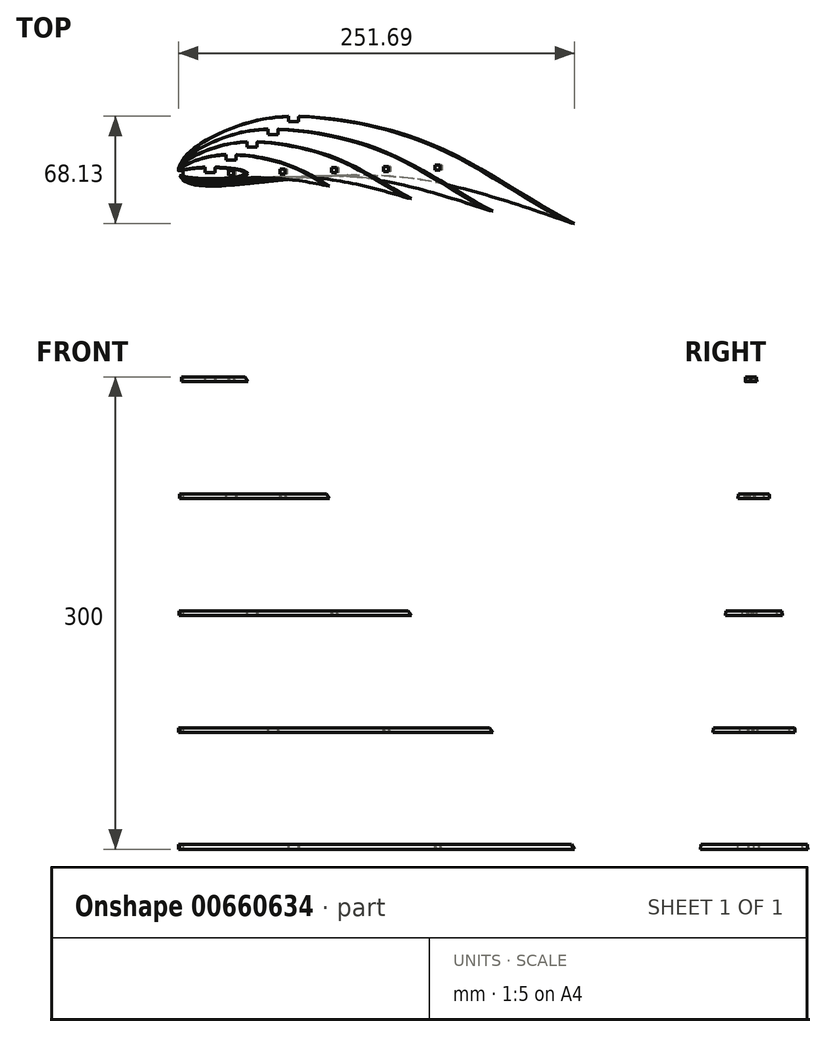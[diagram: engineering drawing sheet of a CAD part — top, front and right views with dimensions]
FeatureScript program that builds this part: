
annotation { "Feature Type Name" : "Feature", "Feature Type Description" : "" }
export const myFeature = defineFeature(function(context is Context, id is Id, definition is map)
    precondition{}
    {
        {
            var Q0;
            Q0=qCreatedBy(makeId("Top.planeOp"),FACE);
            var sketch = newSketch(context, id + "F0", { "sketchPlane" : qUnion([Q0])});
            skLineSegment(sketch, "E0", {"start": v(2.33, 8.6) * mm, "end": v(8.41, 14.52) * mm});
            skLineSegment(sketch, "E1", {"start": v(8.41, 14.52) * mm, "end": v(11.57, 17.3) * mm});
            skLineSegment(sketch, "E2", {"start": v(11.57, 17.3) * mm, "end": v(15.59, 20.39) * mm});
            skLineSegment(sketch, "E3", {"start": v(15.59, 20.39) * mm, "end": v(18.37, 22.2) * mm});
            skLineSegment(sketch, "E4", {"start": v(18.37, 22.2) * mm, "end": v(22.04, 24.25) * mm});
            skLineSegment(sketch, "E5", {"start": v(22.04, 24.25) * mm, "end": v(25.86, 26.05) * mm});
            skLineSegment(sketch, "E6", {"start": v(25.86, 26.05) * mm, "end": v(29.8, 27.65) * mm});
            skLineSegment(sketch, "E7", {"start": v(29.8, 27.65) * mm, "end": v(33.82, 29.05) * mm});
            skLineSegment(sketch, "E8", {"start": v(33.82, 29.05) * mm, "end": v(38.41, 30.45) * mm});
            skLineSegment(sketch, "E9", {"start": v(38.41, 30.45) * mm, "end": v(41.99, 31.4) * mm});
            skLineSegment(sketch, "E10", {"start": v(41.99, 31.4) * mm, "end": v(46.1, 32.39) * mm});
            skLineSegment(sketch, "E11", {"start": v(46.1, 32.39) * mm, "end": v(50.24, 33.24) * mm});
            skLineSegment(sketch, "E12", {"start": v(50.24, 33.24) * mm, "end": v(54.39, 33.98) * mm});
            skLineSegment(sketch, "E13", {"start": v(54.39, 33.98) * mm, "end": v(58.55, 34.6) * mm});
            skLineSegment(sketch, "E14", {"start": v(58.55, 34.6) * mm, "end": v(62.73, 35.1) * mm});
            skLineSegment(sketch, "E15", {"start": v(62.73, 35.1) * mm, "end": v(68.1, 35.6) * mm});
            skLineSegment(sketch, "E16", {"start": v(68.1, 35.6) * mm, "end": v(79.58, 36.1) * mm});
            skLineSegment(sketch, "E17", {"start": v(79.58, 36.1) * mm, "end": v(88.03, 36) * mm});
            skLineSegment(sketch, "E18", {"start": v(88.03, 36) * mm, "end": v(96.45, 35.47) * mm});
            skLineSegment(sketch, "E19", {"start": v(96.45, 35.47) * mm, "end": v(102.22, 34.87) * mm});
            skLineSegment(sketch, "E20", {"start": v(102.22, 34.87) * mm, "end": v(113.1, 33.19) * mm});
            skLineSegment(sketch, "E21", {"start": v(113.1, 33.19) * mm, "end": v(121.32, 31.46) * mm});
            skLineSegment(sketch, "E22", {"start": v(121.32, 31.46) * mm, "end": v(129.5, 29.38) * mm});
            skLineSegment(sketch, "E23", {"start": v(129.5, 29.38) * mm, "end": v(137.56, 27.01) * mm});
            skLineSegment(sketch, "E24", {"start": v(137.56, 27.01) * mm, "end": v(145.85, 24.26) * mm});
            skLineSegment(sketch, "E25", {"start": v(145.85, 24.26) * mm, "end": v(153.9, 21.27) * mm});
            skLineSegment(sketch, "E26", {"start": v(153.9, 21.27) * mm, "end": v(161.71, 18.03) * mm});
            skLineSegment(sketch, "E27", {"start": v(161.71, 18.03) * mm, "end": v(165.5, 16.3) * mm});
            skLineSegment(sketch, "E28", {"start": v(165.5, 16.3) * mm, "end": v(169.18, 14.54) * mm});
            skLineSegment(sketch, "E29", {"start": v(169.18, 14.54) * mm, "end": v(171.67, 13.27) * mm});
            skLineSegment(sketch, "E30", {"start": v(171.67, 13.27) * mm, "end": v(176.2, 10.83) * mm});
            skLineSegment(sketch, "E31", {"start": v(176.2, 10.83) * mm, "end": v(182.99, 6.87) * mm});
            skLineSegment(sketch, "E32", {"start": v(182.99, 6.87) * mm, "end": v(186.43, 4.79) * mm});
            skLineSegment(sketch, "E33", {"start": v(186.43, 4.79) * mm, "end": v(190, 2.63) * mm});
            skLineSegment(sketch, "E34", {"start": v(190, 2.63) * mm, "end": v(193.71, 0.38) * mm});
            skLineSegment(sketch, "E35", {"start": v(193.71, 0.38) * mm, "end": v(197.65, -1.97) * mm});
            skLineSegment(sketch, "E36", {"start": v(197.65, -1.97) * mm, "end": v(201.86, -4.4) * mm});
            skLineSegment(sketch, "E37", {"start": v(201.86, -4.4) * mm, "end": v(206.39, -6.94) * mm});
            skLineSegment(sketch, "E38", {"start": v(206.39, -6.94) * mm, "end": v(211.14, -9.55) * mm});
            skLineSegment(sketch, "E39", {"start": v(211.14, -9.55) * mm, "end": v(216.03, -12.18) * mm});
            skLineSegment(sketch, "E40", {"start": v(216.03, -12.18) * mm, "end": v(225.86, -17.37) * mm});
            skLineSegment(sketch, "E41", {"start": v(225.86, -17.37) * mm, "end": v(230.6, -19.86) * mm});
            skLineSegment(sketch, "E42", {"start": v(230.6, -19.86) * mm, "end": v(235.09, -22.21) * mm});
            skLineSegment(sketch, "E43", {"start": v(235.09, -22.21) * mm, "end": v(239.25, -24.4) * mm});
            skLineSegment(sketch, "E44", {"start": v(239.25, -24.4) * mm, "end": v(241.17, -25.43) * mm});
            skLineSegment(sketch, "E45", {"start": v(241.17, -25.43) * mm, "end": v(242.98, -26.4) * mm});
            skLineSegment(sketch, "E46", {"start": v(242.98, -26.4) * mm, "end": v(244.65, -27.3) * mm});
            skLineSegment(sketch, "E47", {"start": v(244.65, -27.3) * mm, "end": v(246.18, -28.14) * mm});
            skLineSegment(sketch, "E48", {"start": v(246.18, -28.14) * mm, "end": v(247.55, -28.91) * mm});
            skLineSegment(sketch, "E49", {"start": v(247.55, -28.91) * mm, "end": v(248.75, -29.6) * mm});
            skLineSegment(sketch, "E50", {"start": v(248.75, -29.6) * mm, "end": v(249.78, -30.22) * mm});
            skLineSegment(sketch, "E51", {"start": v(249.78, -30.22) * mm, "end": v(250.61, -30.75) * mm});
            skLineSegment(sketch, "E52", {"start": v(250.61, -30.75) * mm, "end": v(251.25, -31.2) * mm});
            skLineSegment(sketch, "E53", {"start": v(251.25, -31.2) * mm, "end": v(251.66, -31.54) * mm});
            skLineSegment(sketch, "E54", {"start": v(251.66, -31.54) * mm, "end": v(251.85, -31.8) * mm});
            skLineSegment(sketch, "E55", {"start": v(251.85, -31.8) * mm, "end": v(251.8, -31.94) * mm});
            skLineSegment(sketch, "E56", {"start": v(251.8, -31.94) * mm, "end": v(251.53, -31.99) * mm});
            skLineSegment(sketch, "E57", {"start": v(251.53, -31.99) * mm, "end": v(251.03, -31.94) * mm});
            skLineSegment(sketch, "E58", {"start": v(251.03, -31.94) * mm, "end": v(250.33, -31.8) * mm});
            skLineSegment(sketch, "E59", {"start": v(250.33, -31.8) * mm, "end": v(249.42, -31.58) * mm});
            skLineSegment(sketch, "E60", {"start": v(249.42, -31.58) * mm, "end": v(248.33, -31.28) * mm});
            skLineSegment(sketch, "E61", {"start": v(248.33, -31.28) * mm, "end": v(247.05, -30.9) * mm});
            skLineSegment(sketch, "E62", {"start": v(247.05, -30.9) * mm, "end": v(245.61, -30.45) * mm});
            skLineSegment(sketch, "E63", {"start": v(245.61, -30.45) * mm, "end": v(244.01, -29.93) * mm});
            skLineSegment(sketch, "E64", {"start": v(244.01, -29.93) * mm, "end": v(242.26, -29.36) * mm});
            skLineSegment(sketch, "E65", {"start": v(242.26, -29.36) * mm, "end": v(240.37, -28.72) * mm});
            skLineSegment(sketch, "E66", {"start": v(240.37, -28.72) * mm, "end": v(238.36, -28.04) * mm});
            skLineSegment(sketch, "E67", {"start": v(238.36, -28.04) * mm, "end": v(236.22, -27.3) * mm});
            skLineSegment(sketch, "E68", {"start": v(236.22, -27.3) * mm, "end": v(231.64, -25.73) * mm});
            skLineSegment(sketch, "E69", {"start": v(231.64, -25.73) * mm, "end": v(226.71, -24.02) * mm});
            skLineSegment(sketch, "E70", {"start": v(226.71, -24.02) * mm, "end": v(221.51, -22.21) * mm});
            skLineSegment(sketch, "E71", {"start": v(221.51, -22.21) * mm, "end": v(210.63, -18.5) * mm});
            skLineSegment(sketch, "E72", {"start": v(210.63, -18.5) * mm, "end": v(199.66, -14.88) * mm});
            skLineSegment(sketch, "E73", {"start": v(199.66, -14.88) * mm, "end": v(192.04, -12.5) * mm});
            skLineSegment(sketch, "E74", {"start": v(192.04, -12.5) * mm, "end": v(189.23, -11.66) * mm});
            skLineSegment(sketch, "E75", {"start": v(189.23, -11.66) * mm, "end": v(184.37, -10.28) * mm});
            skLineSegment(sketch, "E76", {"start": v(184.37, -10.28) * mm, "end": v(179.72, -9.04) * mm});
            skLineSegment(sketch, "E77", {"start": v(179.72, -9.04) * mm, "end": v(175.27, -7.93) * mm});
            skLineSegment(sketch, "E78", {"start": v(175.27, -7.93) * mm, "end": v(170.98, -6.95) * mm});
            skLineSegment(sketch, "E79", {"start": v(170.98, -6.95) * mm, "end": v(166.84, -6.1) * mm});
            skLineSegment(sketch, "E80", {"start": v(166.84, -6.1) * mm, "end": v(162.81, -5.34) * mm});
            skLineSegment(sketch, "E81", {"start": v(162.81, -5.34) * mm, "end": v(158.88, -4.69) * mm});
            skLineSegment(sketch, "E82", {"start": v(158.88, -4.69) * mm, "end": v(155.02, -4.13) * mm});
            skLineSegment(sketch, "E83", {"start": v(155.02, -4.13) * mm, "end": v(147.4, -3.25) * mm});
            skLineSegment(sketch, "E84", {"start": v(147.4, -3.25) * mm, "end": v(136.58, -2.44) * mm});
            skLineSegment(sketch, "E85", {"start": v(136.58, -2.44) * mm, "end": v(131.91, -2.2) * mm});
            skLineSegment(sketch, "E86", {"start": v(131.91, -2.2) * mm, "end": v(123.8, -1.95) * mm});
            skLineSegment(sketch, "E87", {"start": v(123.8, -1.95) * mm, "end": v(115.47, -1.84) * mm});
            skLineSegment(sketch, "E88", {"start": v(115.47, -1.84) * mm, "end": v(106.97, -1.9) * mm});
            skLineSegment(sketch, "E89", {"start": v(106.97, -1.9) * mm, "end": v(98.37, -2.09) * mm});
            skLineSegment(sketch, "E90", {"start": v(98.37, -2.09) * mm, "end": v(89.7, -2.43) * mm});
            skLineSegment(sketch, "E91", {"start": v(89.7, -2.43) * mm, "end": v(80.87, -2.93) * mm});
            skLineSegment(sketch, "E92", {"start": v(80.87, -2.93) * mm, "end": v(72.44, -3.54) * mm});
            skLineSegment(sketch, "E93", {"start": v(72.44, -3.54) * mm, "end": v(63.9, -4.27) * mm});
            skLineSegment(sketch, "E94", {"start": v(63.9, -4.27) * mm, "end": v(55.48, -5.1) * mm});
            skLineSegment(sketch, "E95", {"start": v(55.48, -5.1) * mm, "end": v(47.2, -6) * mm});
            skLineSegment(sketch, "E96", {"start": v(47.2, -6) * mm, "end": v(37.92, -7.1) * mm});
            skLineSegment(sketch, "E97", {"start": v(37.92, -7.1) * mm, "end": v(31.05, -7.9) * mm});
            skLineSegment(sketch, "E98", {"start": v(31.05, -7.9) * mm, "end": v(27.01, -8.21) * mm});
            skLineSegment(sketch, "E99", {"start": v(27.01, -8.21) * mm, "end": v(22.87, -8.35) * mm});
            skLineSegment(sketch, "E100", {"start": v(22.87, -8.35) * mm, "end": v(18.58, -8.21) * mm});
            skLineSegment(sketch, "E101", {"start": v(18.58, -8.21) * mm, "end": v(16.35, -8.02) * mm});
            skLineSegment(sketch, "E102", {"start": v(16.35, -8.02) * mm, "end": v(14.07, -7.74) * mm});
            skLineSegment(sketch, "E103", {"start": v(14.07, -7.74) * mm, "end": v(11.66, -7.35) * mm});
            skLineSegment(sketch, "E104", {"start": v(11.66, -7.35) * mm, "end": v(9.33, -6.86) * mm});
            skLineSegment(sketch, "E105", {"start": v(9.33, -6.86) * mm, "end": v(6.98, -6.22) * mm});
            skLineSegment(sketch, "E106", {"start": v(6.98, -6.22) * mm, "end": v(4.79, -5.42) * mm});
            skLineSegment(sketch, "E107", {"start": v(4.79, -5.42) * mm, "end": v(2.88, -4.42) * mm});
            skLineSegment(sketch, "E108", {"start": v(2.88, -4.42) * mm, "end": v(2.07, -3.84) * mm});
            skLineSegment(sketch, "E109", {"start": v(2.07, -3.84) * mm, "end": v(1.37, -3.2) * mm});
            skLineSegment(sketch, "E110", {"start": v(1.37, -3.2) * mm, "end": v(0.8, -2.5) * mm});
            skLineSegment(sketch, "E111", {"start": v(0.8, -2.5) * mm, "end": v(0.37, -1.7) * mm});
            skLineSegment(sketch, "E112", {"start": v(0.37, -1.7) * mm, "end": v(0.12, -0.9) * mm});
            skLineSegment(sketch, "E113", {"start": v(0.12, -0.9) * mm, "end": v(0, 0) * mm});
            skLineSegment(sketch, "E114", {"start": v(0, 0) * mm, "end": v(0, 0.95) * mm});
            skLineSegment(sketch, "E115", {"start": v(0, 0.95) * mm, "end": v(0.13, 1.96) * mm});
            skLineSegment(sketch, "E116", {"start": v(0.13, 1.96) * mm, "end": v(0.65, 4.08) * mm});
            skLineSegment(sketch, "E117", {"start": v(0.65, 4.08) * mm, "end": v(1.43, 6.32) * mm});
            skLineSegment(sketch, "E118", {"start": v(1.43, 6.32) * mm, "end": v(2.33, 8.6) * mm});
            skSolve(sketch);
        }
        {
            var Q0;
            Q0=qCreatedBy(makeId("Top.planeOp"),FACE);
            var sketch = newSketch(context, id + "F1", { "sketchPlane" : qUnion([Q0])});
            skPoint(sketch, "E119.0", {"position": v(0, 0) * mm});
            skPoint(sketch, "E119.1", {"position": v(0.65, 4.08) * mm});
            skPoint(sketch, "E119.2", {"position": v(8.41, 14.52) * mm});
            skPoint(sketch, "E119.3", {"position": v(41.99, 31.4) * mm});
            skPoint(sketch, "E119.4", {"position": v(79.58, 36.1) * mm});
            skPoint(sketch, "E119.5", {"position": v(161.71, 18.03) * mm});
            skPoint(sketch, "E119.6", {"position": v(251.8, -31.94) * mm});
            skPoint(sketch, "E119.7", {"position": v(155.02, -4.13) * mm});
            skPoint(sketch, "E119.8", {"position": v(80.87, -2.93) * mm});
            skPoint(sketch, "E119.9", {"position": v(31.05, -7.9) * mm});
            skPoint(sketch, "E119.10", {"position": v(16.35, -8.02) * mm});
            skPoint(sketch, "E119.11", {"position": v(4.79, -5.42) * mm});
            skFitSpline(sketch, "E120", {"points": [v(0, 0) * mm, v(0.65, 4.08) * mm, v(8.41, 14.52) * mm, v(41.99, 31.4) * mm, v(79.58, 36.1) * mm, v(161.71, 18.03) * mm, v(251.8, -31.94) * mm], "startDerivative": vector(3.48, 68.82) * mm, "endDerivative": vector(318.06, -154.93) * mm});
            skFitSpline(sketch, "E121", {"points": [v(0, 0) * mm, v(4.79, -5.42) * mm, v(16.35, -8.02) * mm, v(31.05, -7.9) * mm, v(80.87, -2.93) * mm, v(155.02, -4.13) * mm, v(251.8, -31.94) * mm], "startDerivative": vector(50.07, -81.16) * mm, "endDerivative": vector(353.4, -122.9) * mm});
            skSolve(sketch);
        }
        {
            var Q0;
            Q0=qCreatedBy(makeId("Top.planeOp"),FACE);
            cPlane(context, id + "F2", {"entities" : qUnion([Q0]), "cplaneType" : CPlaneType.OFFSET, "offset" : 300 * mm, "width" : 150 * mm, "height" : 150 * mm});
        }
        {
            var Q0;
            Q0=qCreatedBy(id+"F2.planeOp",FACE);
            var sketch = newSketch(context, id + "F3", { "sketchPlane" : qUnion([Q0])});
            skLineSegment(sketch, "E122", {"start": v(0, 0) * mm, "end": v(1, 0.95) * mm});
            skLineSegment(sketch, "E123", {"start": v(1, 0.95) * mm, "end": v(1.3, 1.17) * mm});
            skLineSegment(sketch, "E124", {"start": v(1.3, 1.17) * mm, "end": v(2.15, 1.62) * mm});
            skLineSegment(sketch, "E125", {"start": v(2.15, 1.62) * mm, "end": v(3.47, 2) * mm});
            skLineSegment(sketch, "E126", {"start": v(3.47, 2) * mm, "end": v(4.97, 2.25) * mm});
            skLineSegment(sketch, "E127", {"start": v(4.97, 2.25) * mm, "end": v(7.58, 2.65) * mm});
            skLineSegment(sketch, "E128", {"start": v(7.58, 2.65) * mm, "end": v(10.6, 3.05) * mm});
            skLineSegment(sketch, "E129", {"start": v(10.6, 3.05) * mm, "end": v(12.97, 3.26) * mm});
            skLineSegment(sketch, "E130", {"start": v(12.97, 3.26) * mm, "end": v(17.49, 3.46) * mm});
            skLineSegment(sketch, "E131", {"start": v(17.49, 3.46) * mm, "end": v(21.17, 3.51) * mm});
            skLineSegment(sketch, "E132", {"start": v(21.17, 3.51) * mm, "end": v(24.84, 3.46) * mm});
            skLineSegment(sketch, "E133", {"start": v(24.84, 3.46) * mm, "end": v(29.33, 3.26) * mm});
            skLineSegment(sketch, "E134", {"start": v(29.33, 3.26) * mm, "end": v(31.72, 3.05) * mm});
            skLineSegment(sketch, "E135", {"start": v(31.72, 3.05) * mm, "end": v(34.82, 2.65) * mm});
            skLineSegment(sketch, "E136", {"start": v(34.82, 2.65) * mm, "end": v(37.36, 2.25) * mm});
            skLineSegment(sketch, "E137", {"start": v(37.36, 2.25) * mm, "end": v(38.72, 2) * mm});
            skLineSegment(sketch, "E138", {"start": v(38.72, 2) * mm, "end": v(40.02, 1.62) * mm});
            skLineSegment(sketch, "E139", {"start": v(40.02, 1.62) * mm, "end": v(41.03, 1.17) * mm});
            skLineSegment(sketch, "E140", {"start": v(41.03, 1.17) * mm, "end": v(41.44, 0.95) * mm});
            skLineSegment(sketch, "E141", {"start": v(41.44, 0.95) * mm, "end": v(42.06, 0.5) * mm});
            skLineSegment(sketch, "E142", {"start": v(42.06, 0.5) * mm, "end": v(42.25, 0.25) * mm});
            skLineSegment(sketch, "E143", {"start": v(42.25, 0.25) * mm, "end": v(42.33, 0) * mm});
            skLineSegment(sketch, "E144", {"start": v(42.33, 0) * mm, "end": v(42.25, -0.25) * mm});
            skLineSegment(sketch, "E145", {"start": v(42.25, -0.25) * mm, "end": v(42.06, -0.5) * mm});
            skLineSegment(sketch, "E146", {"start": v(42.06, -0.5) * mm, "end": v(41.44, -0.95) * mm});
            skLineSegment(sketch, "E147", {"start": v(41.44, -0.95) * mm, "end": v(41.03, -1.17) * mm});
            skLineSegment(sketch, "E148", {"start": v(41.03, -1.17) * mm, "end": v(40.02, -1.62) * mm});
            skLineSegment(sketch, "E149", {"start": v(40.02, -1.62) * mm, "end": v(38.72, -2) * mm});
            skLineSegment(sketch, "E150", {"start": v(38.72, -2) * mm, "end": v(37.36, -2.25) * mm});
            skLineSegment(sketch, "E151", {"start": v(37.36, -2.25) * mm, "end": v(34.82, -2.65) * mm});
            skLineSegment(sketch, "E152", {"start": v(34.82, -2.65) * mm, "end": v(31.72, -3.05) * mm});
            skLineSegment(sketch, "E153", {"start": v(31.72, -3.05) * mm, "end": v(29.33, -3.26) * mm});
            skLineSegment(sketch, "E154", {"start": v(29.33, -3.26) * mm, "end": v(24.84, -3.46) * mm});
            skLineSegment(sketch, "E155", {"start": v(24.84, -3.46) * mm, "end": v(21.17, -3.51) * mm});
            skLineSegment(sketch, "E156", {"start": v(21.17, -3.51) * mm, "end": v(17.49, -3.46) * mm});
            skLineSegment(sketch, "E157", {"start": v(17.49, -3.46) * mm, "end": v(12.97, -3.26) * mm});
            skLineSegment(sketch, "E158", {"start": v(12.97, -3.26) * mm, "end": v(10.6, -3.05) * mm});
            skLineSegment(sketch, "E159", {"start": v(10.6, -3.05) * mm, "end": v(7.58, -2.65) * mm});
            skLineSegment(sketch, "E160", {"start": v(7.58, -2.65) * mm, "end": v(4.97, -2.25) * mm});
            skLineSegment(sketch, "E161", {"start": v(4.97, -2.25) * mm, "end": v(3.47, -2) * mm});
            skLineSegment(sketch, "E162", {"start": v(3.47, -2) * mm, "end": v(2.15, -1.62) * mm});
            skLineSegment(sketch, "E163", {"start": v(2.15, -1.62) * mm, "end": v(1.3, -1.17) * mm});
            skLineSegment(sketch, "E164", {"start": v(1.3, -1.17) * mm, "end": v(1, -0.95) * mm});
            skLineSegment(sketch, "E165", {"start": v(1, -0.95) * mm, "end": v(0, 0) * mm});
            skPoint(sketch, "E166.9", {"position": v(0, 0) * mm});
            skSolve(sketch);
        }
        {
            var Q0;
            Q0=qCreatedBy(id+"F2.planeOp",FACE);
            var sketch = newSketch(context, id + "F4", { "sketchPlane" : qUnion([Q0])});
            skPoint(sketch, "E167.0", {"position": v(0, 0) * mm});
            skPoint(sketch, "E167.1", {"position": v(2.15, 1.62) * mm});
            skPoint(sketch, "E167.2", {"position": v(12.97, 3.26) * mm});
            skPoint(sketch, "E167.3", {"position": v(24.84, 3.46) * mm});
            skPoint(sketch, "E167.4", {"position": v(40.02, 1.62) * mm});
            skPoint(sketch, "E167.5", {"position": v(42.33, 0) * mm});
            skPoint(sketch, "E167.6", {"position": v(40.02, -1.62) * mm});
            skPoint(sketch, "E167.7", {"position": v(24.84, -3.46) * mm});
            skPoint(sketch, "E167.8", {"position": v(12.97, -3.26) * mm});
            skPoint(sketch, "E167.9", {"position": v(2.15, -1.62) * mm});
            skFitSpline(sketch, "E168", {"points": [v(0, 0) * mm, v(2.43, 1.62) * mm, v(12.97, 3.26) * mm, v(24.84, 3.46) * mm, v(40.02, 1.62) * mm, v(42.33, 0) * mm], "startDerivative": vector(15.13, 14.18) * mm, "endDerivative": vector(13.02, -14.35) * mm});
            skFitSpline(sketch, "E169", {"points": [v(0, 0) * mm, v(2.15, -1.62) * mm, v(12.97, -3.26) * mm, v(24.84, -3.46) * mm, v(40.02, -1.62) * mm, v(42.33, 0) * mm], "startDerivative": vector(13.24, -14.8) * mm, "endDerivative": vector(12.97, 14.32) * mm});
            skSolve(sketch);
        }
        {
            var Q0;
            Q0=makeQuery(id+"F1.imprint","IMPRINT",FACE,{"disambiguationData":[TD([[makeQuery(id+"F1.imprint","IMPRINT",EDGE,{"derivedFrom":sQuery(id+"F1.wireOp",EDGE,"E120")}),-1.0]])]});
            var Q1;
            Q1=makeQuery(id+"F4.imprint","IMPRINT",FACE,{"disambiguationData":[TD([[makeQuery(id+"F4.imprint","IMPRINT",EDGE,{"derivedFrom":sQuery(id+"F4.wireOp",EDGE,"E168")}),-1.0]])]});
            loft(context, id + "F5", {"sheetProfilesArray" : [{ "sheetProfileEntities" : qUnion([Q0]) }, { "sheetProfileEntities" : qUnion([Q1]) }]});
        }
        {
            var Q0;
            Q0=qCreatedBy(makeId("Front.planeOp"),FACE);
            var sketch = newSketch(context, id + "F6", { "sketchPlane" : qUnion([Q0])});
            skLineSegment(sketch, "E170", {"start": v(0, 0) * mm, "end": v(0, 3) * mm, "construction": true});
            skLineSegment(sketch, "E171.bottom", {"start": v(0, 3) * mm, "end": v(297.86, 3) * mm});
            skLineSegment(sketch, "E171.top", {"start": v(0, 74.25) * mm, "end": v(297.86, 74.25) * mm});
            skLineSegment(sketch, "E171.left", {"start": v(0, 3) * mm, "end": v(0, 74.25) * mm});
            skLineSegment(sketch, "E171.right", {"start": v(297.86, 3) * mm, "end": v(297.86, 74.25) * mm});
            skLineSegment(sketch, "E172", {"start": v(0, 74.25) * mm, "end": v(0, 77.25) * mm, "construction": true});
            skLineSegment(sketch, "E173.bottom", {"start": v(0, 77.25) * mm, "end": v(251.76, 77.25) * mm});
            skLineSegment(sketch, "E173.top", {"start": v(0, 148.5) * mm, "end": v(251.76, 148.5) * mm});
            skLineSegment(sketch, "E173.left", {"start": v(0, 77.25) * mm, "end": v(0, 148.5) * mm});
            skLineSegment(sketch, "E173.right", {"start": v(251.76, 77.25) * mm, "end": v(251.76, 148.5) * mm});
            skLineSegment(sketch, "E174", {"start": v(0, 148.5) * mm, "end": v(0, 151.5) * mm, "construction": true});
            skLineSegment(sketch, "E175.bottom", {"start": v(0, 151.5) * mm, "end": v(163.96, 151.5) * mm});
            skLineSegment(sketch, "E175.top", {"start": v(0, 222.75) * mm, "end": v(163.96, 222.75) * mm});
            skLineSegment(sketch, "E175.left", {"start": v(0, 151.5) * mm, "end": v(0, 222.75) * mm});
            skLineSegment(sketch, "E175.right", {"start": v(163.96, 151.5) * mm, "end": v(163.96, 222.75) * mm});
            skLineSegment(sketch, "E176", {"start": v(0, 222.75) * mm, "end": v(0, 225.75) * mm});
            skLineSegment(sketch, "E177.bottom", {"start": v(0, 225.75) * mm, "end": v(157.2, 225.75) * mm});
            skLineSegment(sketch, "E177.top", {"start": v(0, 297) * mm, "end": v(157.2, 297) * mm});
            skLineSegment(sketch, "E177.left", {"start": v(0, 225.75) * mm, "end": v(0, 297) * mm});
            skLineSegment(sketch, "E177.right", {"start": v(157.2, 225.75) * mm, "end": v(157.2, 297) * mm});
            skSolve(sketch);
        }
        {
            var Q0;
            Q0=makeQuery(id+"F6.imprint","IMPRINT",FACE,{"disambiguationData":[TD([[makeQuery(id+"F6.imprint","IMPRINT",EDGE,{"derivedFrom":sQuery(id+"F6.wireOp",EDGE,"E177.bottom")}),1.0]])]});
            var Q1;
            Q1=makeQuery(id+"F6.imprint","IMPRINT",FACE,{"disambiguationData":[TD([[makeQuery(id+"F6.imprint","IMPRINT",EDGE,{"derivedFrom":sQuery(id+"F6.wireOp",EDGE,"E175.bottom")}),1.0]])]});
            var Q2;
            Q2=makeQuery(id+"F6.imprint","IMPRINT",FACE,{"disambiguationData":[TD([[makeQuery(id+"F6.imprint","IMPRINT",EDGE,{"derivedFrom":sQuery(id+"F6.wireOp",EDGE,"E173.bottom")}),1.0]])]});
            var Q3;
            Q3=makeQuery(id+"F6.imprint","IMPRINT",FACE,{"disambiguationData":[TD([[makeQuery(id+"F6.imprint","IMPRINT",EDGE,{"derivedFrom":sQuery(id+"F6.wireOp",EDGE,"E171.bottom")}),1.0]])]});
            extrude(context, id + "F7", {"entities" : qUnion([Q0, Q1, Q2, Q3]), "operationType" : NewBodyOperationType.REMOVE, "depth" : 50 * mm, "offsetDistance" : 25 * mm, "hasSecondDirection" : true, "secondDirectionOppositeDirection" : true, "secondDirectionDepth" : 50 * mm});
        }
        {
            var Q0;
            Q0=qCreatedBy(makeId("Top.planeOp"),FACE);
            var sketch = newSketch(context, id + "F8", { "sketchPlane" : qUnion([Q0])});
            skLineSegment(sketch, "E178", {"start": v(3.18, 0) * mm, "end": v(3.18, 1.59) * mm});
            skLineSegment(sketch, "E179", {"start": v(3.18, 0) * mm, "end": v(3.18, -1.59) * mm});
            skLineSegment(sketch, "E180", {"start": v(3.18, -1.59) * mm, "end": v(0, -1.59) * mm});
            skLineSegment(sketch, "E181", {"start": v(0, -1.59) * mm, "end": v(0, 1.59) * mm});
            skLineSegment(sketch, "E182", {"start": v(0, 1.59) * mm, "end": v(3.18, 1.59) * mm});
            skLineSegment(sketch, "E183", {"start": v(0, 0) * mm, "end": v(3.18, 0) * mm, "construction": true});
            skLineSegment(sketch, "E184.top", {"start": v(0, -1.59) * mm, "end": v(3.18, -1.59) * mm});
            skLineSegment(sketch, "E184.left", {"start": v(0, 1.59) * mm, "end": v(0, -1.59) * mm});
            skLineSegment(sketch, "E184.right", {"start": v(3.18, 1.59) * mm, "end": v(3.18, -1.59) * mm});
            skSolve(sketch);
        }
        {
            var Q0;
            Q0=makeQuery(id+"F8.imprint","IMPRINT",FACE,{"disambiguationData":[TD([[makeQuery(id+"F8.imprint","IMPRINT",EDGE,{"derivedFrom":sQuery(id+"F8.wireOp",EDGE,"E182")}),-1.0]])]});
            extrude(context, id + "F9", {"entities" : qUnion([Q0]), "operationType" : NewBodyOperationType.REMOVE, "depth" : 300 * mm, "offsetDistance" : 25 * mm});
        }
        {
            var Q0;
            Q0=makeQuery(id+"F5.opLoft","CAP_FACE",FACE,{"disambiguationData":[OSD([makeQuery(id+"F1.imprint","IMPRINT",FACE,{"disambiguationData":[TD([[makeQuery(id+"F1.imprint","IMPRINT",EDGE,{"derivedFrom":sQuery(id+"F1.wireOp",EDGE,"E120")}),-1.0]])]})])],"isStart":true});
            var sketch = newSketch(context, id + "F10", { "sketchPlane" : qUnion([Q0])});
            skPoint(sketch, "E185", {"position": v(73.91, -36.22) * mm});
            skLineSegment(sketch, "E186", {"start": v(73.91, -36.22) * mm, "end": v(73.91, -33.05) * mm, "construction": true});
            skLineSegment(sketch, "E187", {"start": v(73.91, -33.05) * mm, "end": v(70.74, -33.05) * mm});
            skLineSegment(sketch, "E188", {"start": v(73.91, -33.05) * mm, "end": v(77.09, -33.05) * mm});
            skLineSegment(sketch, "E189", {"start": v(77.09, -33.05) * mm, "end": v(77.09, -36.22) * mm});
            skLineSegment(sketch, "E190", {"start": v(77.09, -36.22) * mm, "end": v(70.74, -36.22) * mm, "construction": true});
            skLineSegment(sketch, "E191", {"start": v(70.74, -36.22) * mm, "end": v(70.74, -33.05) * mm});
            skLineSegment(sketch, "E192", {"start": v(70.74, -36.22) * mm, "end": v(70.74, -37.36) * mm});
            skLineSegment(sketch, "E193", {"start": v(70.74, -37.36) * mm, "end": v(77.09, -37.36) * mm});
            skLineSegment(sketch, "E194", {"start": v(77.09, -37.36) * mm, "end": v(77.09, -36.22) * mm});
            skSolve(sketch);
        }
        {
            var Q0;
            Q0=makeQuery(id+"F5.opLoft","CAP_FACE",FACE,{"disambiguationData":[OSD([makeQuery(id+"F4.imprint","IMPRINT",FACE,{"disambiguationData":[TD([[makeQuery(id+"F4.imprint","IMPRINT",EDGE,{"derivedFrom":sQuery(id+"F4.wireOp",EDGE,"E168")}),-1.0]])]})])],"isStart":true});
            var sketch = newSketch(context, id + "F11", { "sketchPlane" : qUnion([Q0])});
            skFitSpline(sketch, "E195.0", {"points": [v(2.17, 1.59) * mm, v(2.59, 1.78) * mm, v(3.44, 2.08) * mm, v(4.75, 2.41) * mm, v(6.07, 2.68) * mm, v(7.85, 2.98) * mm, v(10.08, 3.26) * mm, v(12.77, 3.53) * mm, v(15.46, 3.73) * mm, v(18.16, 3.86) * mm, v(20.87, 3.9) * mm, v(23.57, 3.84) * mm, v(26.27, 3.73) * mm, v(28.97, 3.56) * mm, v(31.66, 3.34) * mm, v(33.9, 3.1) * mm, v(35.7, 2.87) * mm, v(37.03, 2.66) * mm, v(38.35, 2.43) * mm, v(39.68, 2.14) * mm, v(40.99, 1.8) * mm, v(42.04, 1.4) * mm, v(42.84, 0.99) * mm, v(43.41, 0.6) * mm, v(43.93, 0.16) * mm, v(44.26, -0.16) * mm, v(44.42, -0.32) * mm], "construction": true});
            skLineSegment(sketch, "E196", {"start": v(20.32, 3.88) * mm, "end": v(20.32, 0.7) * mm, "construction": true});
            skLineSegment(sketch, "E197.top", {"start": v(17.14, 0.32) * mm, "end": v(23.88, 0.32) * mm});
            skLineSegment(sketch, "E198", {"start": v(23.88, 3.5) * mm, "end": v(23.88, 0.32) * mm});
            skLineSegment(sketch, "E199", {"start": v(17.14, 3.5) * mm, "end": v(17.14, 0.32) * mm});
            skLineSegment(sketch, "E200", {"start": v(17.14, 3.5) * mm, "end": v(23.88, 3.5) * mm});
            skSolve(sketch);
        }
        {
            var Q0;
            Q0=sQuery(id+"F10.wireOp",VERTEX,"E191.start");
            var Q1;
            Q1=sQuery(id+"F10.wireOp",VERTEX,"E191.end");
            var Q2;
            Q2=sQuery(id+"F11.wireOp",VERTEX,"E199.end");
            cPlane(context, id + "F12", {"entities" : qUnion([Q0, Q1, Q2]), "cplaneType" : CPlaneType.THREE_POINT, "offset" : 25 * mm, "width" : 150 * mm, "height" : 150 * mm});
        }
        {
            var Q0;
            Q0=qCreatedBy(id+"F12.planeOp",FACE);
            var sketch = newSketch(context, id + "F13", { "sketchPlane" : qUnion([Q0])});
            skPoint(sketch, "E201.0", {"position": v(33.05, -12.44) * mm});
            skPoint(sketch, "E201.1", {"position": v(0.32, 292.3) * mm});
            skLineSegment(sketch, "E202", {"start": v(0.32, 292.3) * mm, "end": v(33.05, -12.44) * mm});
            skSolve(sketch);
        }
        {
            var Q0;
            Q0 = qSketchRegion(id + "F10", true);
            var Q1;
            Q1 = qConstructionFilter(qBodyType(qCreatedBy(id + "F10" ,EDGE), BodyType.WIRE), ConstructionObject.NO);
            var Q2;
            Q2=sQuery(id+"F13.wireOp",EDGE,"E202");
            sweep(context, id + "F14", {"operationType" : NewBodyOperationType.REMOVE, "profiles" : qUnion([Q0]), "surfaceProfiles" : qUnion([Q1]), "path" : qUnion([Q2])});
        }
        {
            var Q0;
            Q0=makeQuery(id+"F5.opLoft","CAP_FACE",FACE,{"disambiguationData":[OSD([makeQuery(id+"F1.imprint","IMPRINT",FACE,{"disambiguationData":[TD([[makeQuery(id+"F1.imprint","IMPRINT",EDGE,{"derivedFrom":sQuery(id+"F1.wireOp",EDGE,"E120")}),-1.0]])]})])],"isStart":true});
            var sketch = newSketch(context, id + "F15", { "sketchPlane" : qUnion([Q0])});
            skLineSegment(sketch, "E203.bottom", {"start": v(167.59, -5.18) * mm, "end": v(164.41, -5.18) * mm});
            skLineSegment(sketch, "E203.top", {"start": v(167.59, -2) * mm, "end": v(164.41, -2) * mm});
            skLineSegment(sketch, "E203.left", {"start": v(167.59, -5.18) * mm, "end": v(167.59, -2) * mm});
            skLineSegment(sketch, "E203.right", {"start": v(164.41, -5.18) * mm, "end": v(164.41, -2) * mm});
            skSolve(sketch);
        }
        {
            var Q0;
            Q0=makeQuery(id+"F11.imprint","IMPRINT",FACE,{"disambiguationData":[TD([[makeQuery(id+"F11.imprint","IMPRINT",EDGE,{"derivedFrom":sQuery(id+"F11.wireOp",EDGE,"E197.top")}),-1.0]])]});
            var sketch = newSketch(context, id + "F16", { "sketchPlane" : qUnion([Q0])});
            skLineSegment(sketch, "E204.bottom", {"start": v(31.86, 1.7) * mm, "end": v(35.03, 1.7) * mm});
            skLineSegment(sketch, "E204.top", {"start": v(31.86, -1.48) * mm, "end": v(35.03, -1.48) * mm});
            skLineSegment(sketch, "E204.left", {"start": v(31.86, 1.7) * mm, "end": v(31.86, -1.48) * mm});
            skLineSegment(sketch, "E204.right", {"start": v(35.03, 1.7) * mm, "end": v(35.03, -1.48) * mm});
            skSolve(sketch);
        }
        {
            var Q0;
            Q0 = qSketchRegion(id + "F15", true);
            var Q1;
            Q1 = qSketchRegion(id + "F16", true);
            loft(context, id + "F17", {"operationType" : NewBodyOperationType.REMOVE, "sheetProfilesArray" : [{ "sheetProfileEntities" : qUnion([Q0]) }, { "sheetProfileEntities" : qUnion([Q1]) }]});
        }
        {
            var Q0;
            Q0=makeQuery(id+"F11.imprint","IMPRINT",FACE,{"disambiguationData":[TD([[makeQuery(id+"F11.imprint","IMPRINT",EDGE,{"derivedFrom":sQuery(id+"F11.wireOp",EDGE,"E197.top")}),-1.0]])]});
            var sketch = newSketch(context, id + "F18", { "sketchPlane" : qUnion([Q0])});
            skLineSegment(sketch, "E205.0", {"start": v(17.14, 3.5) * mm, "end": v(17.14, 0.32) * mm});
            skLineSegment(sketch, "E205.1", {"start": v(23.5, 0.32) * mm, "end": v(23.5, 3.51) * mm});
            skLineSegment(sketch, "E205.2", {"start": v(35.03, -1.48) * mm, "end": v(35.03, 1.7) * mm});
            skLineSegment(sketch, "E205.3", {"start": v(31.86, 1.7) * mm, "end": v(31.86, -1.48) * mm});
            skLineSegment(sketch, "E206", {"start": v(31.86, 1.7) * mm, "end": v(35.03, 1.7) * mm});
            skLineSegment(sketch, "E207", {"start": v(35.03, -1.48) * mm, "end": v(31.86, -1.48) * mm});
            skLineSegment(sketch, "E208", {"start": v(17.14, 3.5) * mm, "end": v(17.14, 4.5) * mm});
            skLineSegment(sketch, "E209", {"start": v(17.14, 4.5) * mm, "end": v(23.5, 4.5) * mm});
            skLineSegment(sketch, "E210", {"start": v(23.5, 4.5) * mm, "end": v(23.5, 3.51) * mm});
            skLineSegment(sketch, "E211", {"start": v(17.14, 0.32) * mm, "end": v(23.5, 0.32) * mm});
            skSolve(sketch);
        }
        {
            var Q0;
            Q0=makeQuery(id+"F18.imprint","IMPRINT",FACE,{"disambiguationData":[TD([[makeQuery(id+"F18.imprint","IMPRINT",EDGE,{"derivedFrom":sQuery(id+"F18.wireOp",EDGE,"E205.0")}),1.0]])]});
            var Q1;
            Q1=makeQuery(id+"F18.imprint","IMPRINT",FACE,{"disambiguationData":[TD([[makeQuery(id+"F18.imprint","IMPRINT",EDGE,{"derivedFrom":sQuery(id+"F18.wireOp",EDGE,"E205.2")}),1.0]])]});
            extrude(context, id + "F19", {"entities" : qUnion([Q0, Q1]), "operationType" : NewBodyOperationType.REMOVE, "oppositeDirection" : true, "depth" : 10 * mm, "offsetDistance" : 25 * mm});
        }
        {
            var Q0;
            Q0=makeQuery(id+"F7.boolean.opBoolean","COPY",FACE,{"derivedFrom":makeQuery(id+"F7.opExtrude","SWEPT_FACE",FACE,{"disambiguationData":[OSD([sQuery(id+"F6.wireOp",EDGE,"E177.bottom")])]})});
            var sketch = newSketch(context, id + "F20", { "sketchPlane" : qUnion([Q0])});
            skLineSegment(sketch, "E212.0", {"start": v(30.4, 11.6) * mm, "end": v(30.4, 8.42) * mm});
            skLineSegment(sketch, "E212.1", {"start": v(30.4, 8.42) * mm, "end": v(36.76, 8.42) * mm});
            skLineSegment(sketch, "E212.2", {"start": v(64.66, 2.56) * mm, "end": v(64.66, -0.62) * mm});
            skLineSegment(sketch, "E212.3", {"start": v(67.84, -0.62) * mm, "end": v(67.84, 2.56) * mm});
            skLineSegment(sketch, "E213", {"start": v(30.4, 11.6) * mm, "end": v(30.4, 12.88) * mm});
            skLineSegment(sketch, "E214", {"start": v(30.4, 12.88) * mm, "end": v(36.76, 12.88) * mm});
            skLineSegment(sketch, "E215", {"start": v(36.76, 12.88) * mm, "end": v(36.76, 8.42) * mm});
            skLineSegment(sketch, "E216", {"start": v(64.66, 2.56) * mm, "end": v(67.84, 2.56) * mm});
            skLineSegment(sketch, "E217", {"start": v(67.84, -0.62) * mm, "end": v(64.66, -0.62) * mm});
            skSolve(sketch);
        }
        {
            var Q0;
            Q0=makeQuery(id+"F20.imprint","IMPRINT",FACE,{"disambiguationData":[TD([[makeQuery(id+"F20.imprint","IMPRINT",EDGE,{"derivedFrom":sQuery(id+"F20.wireOp",EDGE,"E212.2")}),1.0]])]});
            var Q1;
            Q1=makeQuery(id+"F20.imprint","IMPRINT",FACE,{"disambiguationData":[TD([[makeQuery(id+"F20.imprint","IMPRINT",EDGE,{"derivedFrom":sQuery(id+"F20.wireOp",EDGE,"E212.0")}),1.0]])]});
            extrude(context, id + "F21", {"entities" : qUnion([Q0, Q1]), "operationType" : NewBodyOperationType.REMOVE, "oppositeDirection" : true, "depth" : 10 * mm, "offsetDistance" : 25 * mm});
        }
        {
            var Q0;
            Q0=makeQuery(id+"F7.boolean.opBoolean","COPY",FACE,{"derivedFrom":makeQuery(id+"F7.opExtrude","SWEPT_FACE",FACE,{"disambiguationData":[OSD([sQuery(id+"F6.wireOp",EDGE,"E175.bottom")])]})});
            var sketch = newSketch(context, id + "F22", { "sketchPlane" : qUnion([Q0])});
            skLineSegment(sketch, "E218.0", {"start": v(43.67, 19.69) * mm, "end": v(43.67, 16.52) * mm});
            skLineSegment(sketch, "E218.1", {"start": v(43.67, 16.52) * mm, "end": v(50.02, 16.52) * mm});
            skLineSegment(sketch, "E218.2", {"start": v(97.47, 3.42) * mm, "end": v(97.47, 0.24) * mm});
            skLineSegment(sketch, "E218.3", {"start": v(100.65, 0.24) * mm, "end": v(100.65, 3.42) * mm});
            skLineSegment(sketch, "E219", {"start": v(43.67, 19.69) * mm, "end": v(43.67, 21.8) * mm});
            skLineSegment(sketch, "E220", {"start": v(43.67, 21.8) * mm, "end": v(50.02, 21.8) * mm});
            skLineSegment(sketch, "E221", {"start": v(50.02, 21.8) * mm, "end": v(50.02, 16.52) * mm});
            skLineSegment(sketch, "E222", {"start": v(97.47, 3.42) * mm, "end": v(100.65, 3.42) * mm});
            skLineSegment(sketch, "E223", {"start": v(100.65, 0.24) * mm, "end": v(97.47, 0.24) * mm});
            skSolve(sketch);
        }
        {
            var Q0;
            Q0=makeQuery(id+"F22.imprint","IMPRINT",FACE,{"disambiguationData":[TD([[makeQuery(id+"F22.imprint","IMPRINT",EDGE,{"derivedFrom":sQuery(id+"F22.wireOp",EDGE,"E218.2")}),1.0]])]});
            var Q1;
            Q1=makeQuery(id+"F22.imprint","IMPRINT",FACE,{"disambiguationData":[TD([[makeQuery(id+"F22.imprint","IMPRINT",EDGE,{"derivedFrom":sQuery(id+"F22.wireOp",EDGE,"E218.0")}),1.0]])]});
            extrude(context, id + "F23", {"entities" : qUnion([Q0, Q1]), "operationType" : NewBodyOperationType.REMOVE, "oppositeDirection" : true, "depth" : 10 * mm, "offsetDistance" : 25 * mm});
        }
        {
            var Q0;
            Q0=makeQuery(id+"F7.boolean.opBoolean","COPY",FACE,{"derivedFrom":makeQuery(id+"F7.opExtrude","SWEPT_FACE",FACE,{"disambiguationData":[OSD([sQuery(id+"F6.wireOp",EDGE,"E173.bottom")])]})});
            var sketch = newSketch(context, id + "F24", { "sketchPlane" : qUnion([Q0])});
            skLineSegment(sketch, "E224.0", {"start": v(56.94, 27.78) * mm, "end": v(56.94, 24.62) * mm});
            skLineSegment(sketch, "E224.1", {"start": v(56.94, 24.62) * mm, "end": v(63.29, 24.62) * mm});
            skLineSegment(sketch, "E224.2", {"start": v(130.28, 4.28) * mm, "end": v(130.28, 1.1) * mm});
            skLineSegment(sketch, "E224.3", {"start": v(133.45, 1.1) * mm, "end": v(133.45, 4.28) * mm});
            skLineSegment(sketch, "E225", {"start": v(56.94, 27.78) * mm, "end": v(56.94, 29.5) * mm});
            skLineSegment(sketch, "E226", {"start": v(56.94, 29.5) * mm, "end": v(63.29, 29.5) * mm});
            skLineSegment(sketch, "E227", {"start": v(63.29, 29.5) * mm, "end": v(63.29, 24.62) * mm});
            skLineSegment(sketch, "E228", {"start": v(133.45, 4.28) * mm, "end": v(130.28, 4.28) * mm});
            skLineSegment(sketch, "E229", {"start": v(133.45, 1.1) * mm, "end": v(130.28, 1.1) * mm});
            skSolve(sketch);
        }
        {
            var Q0;
            Q0=makeQuery(id+"F24.imprint","IMPRINT",FACE,{"disambiguationData":[TD([[makeQuery(id+"F24.imprint","IMPRINT",EDGE,{"derivedFrom":sQuery(id+"F24.wireOp",EDGE,"E224.0")}),1.0]])]});
            var Q1;
            Q1=makeQuery(id+"F24.imprint","IMPRINT",FACE,{"disambiguationData":[TD([[makeQuery(id+"F24.imprint","IMPRINT",EDGE,{"derivedFrom":sQuery(id+"F24.wireOp",EDGE,"E224.2")}),1.0]])]});
            extrude(context, id + "F25", {"entities" : qUnion([Q0, Q1]), "operationType" : NewBodyOperationType.REMOVE, "oppositeDirection" : true, "depth" : 10 * mm, "offsetDistance" : 25 * mm});
        }
        {
            var Q0;
            Q0=makeQuery(id+"F7.boolean.opBoolean","COPY",FACE,{"derivedFrom":makeQuery(id+"F7.opExtrude","SWEPT_FACE",FACE,{"disambiguationData":[OSD([sQuery(id+"F6.wireOp",EDGE,"E171.bottom")])]})});
            var sketch = newSketch(context, id + "F26", { "sketchPlane" : qUnion([Q0])});
            skLineSegment(sketch, "E230.0", {"start": v(70.2, 35.87) * mm, "end": v(70.2, 32.72) * mm});
            skLineSegment(sketch, "E230.1", {"start": v(70.2, 32.72) * mm, "end": v(76.55, 32.72) * mm});
            skLineSegment(sketch, "E230.2", {"start": v(163.09, 5.14) * mm, "end": v(163.09, 1.97) * mm});
            skLineSegment(sketch, "E230.3", {"start": v(166.26, 1.97) * mm, "end": v(166.26, 5.14) * mm});
            skLineSegment(sketch, "E231", {"start": v(70.2, 35.87) * mm, "end": v(70.2, 38.45) * mm});
            skLineSegment(sketch, "E232", {"start": v(70.2, 38.45) * mm, "end": v(76.55, 38.45) * mm});
            skLineSegment(sketch, "E233", {"start": v(76.55, 38.45) * mm, "end": v(76.55, 32.72) * mm});
            skLineSegment(sketch, "E234", {"start": v(163.09, 5.14) * mm, "end": v(166.26, 5.14) * mm});
            skLineSegment(sketch, "E235", {"start": v(166.26, 1.97) * mm, "end": v(163.09, 1.97) * mm});
            skSolve(sketch);
        }
        {
            var Q0;
            Q0=makeQuery(id+"F26.imprint","IMPRINT",FACE,{"disambiguationData":[TD([[makeQuery(id+"F26.imprint","IMPRINT",EDGE,{"derivedFrom":sQuery(id+"F26.wireOp",EDGE,"E230.2")}),1.0]])]});
            var Q1;
            Q1=makeQuery(id+"F26.imprint","IMPRINT",FACE,{"disambiguationData":[TD([[makeQuery(id+"F26.imprint","IMPRINT",EDGE,{"derivedFrom":sQuery(id+"F26.wireOp",EDGE,"E230.0")}),1.0]])]});
            extrude(context, id + "F27", {"entities" : qUnion([Q0, Q1]), "operationType" : NewBodyOperationType.REMOVE, "oppositeDirection" : true, "depth" : 10 * mm, "offsetDistance" : 25 * mm});
        }
    });
